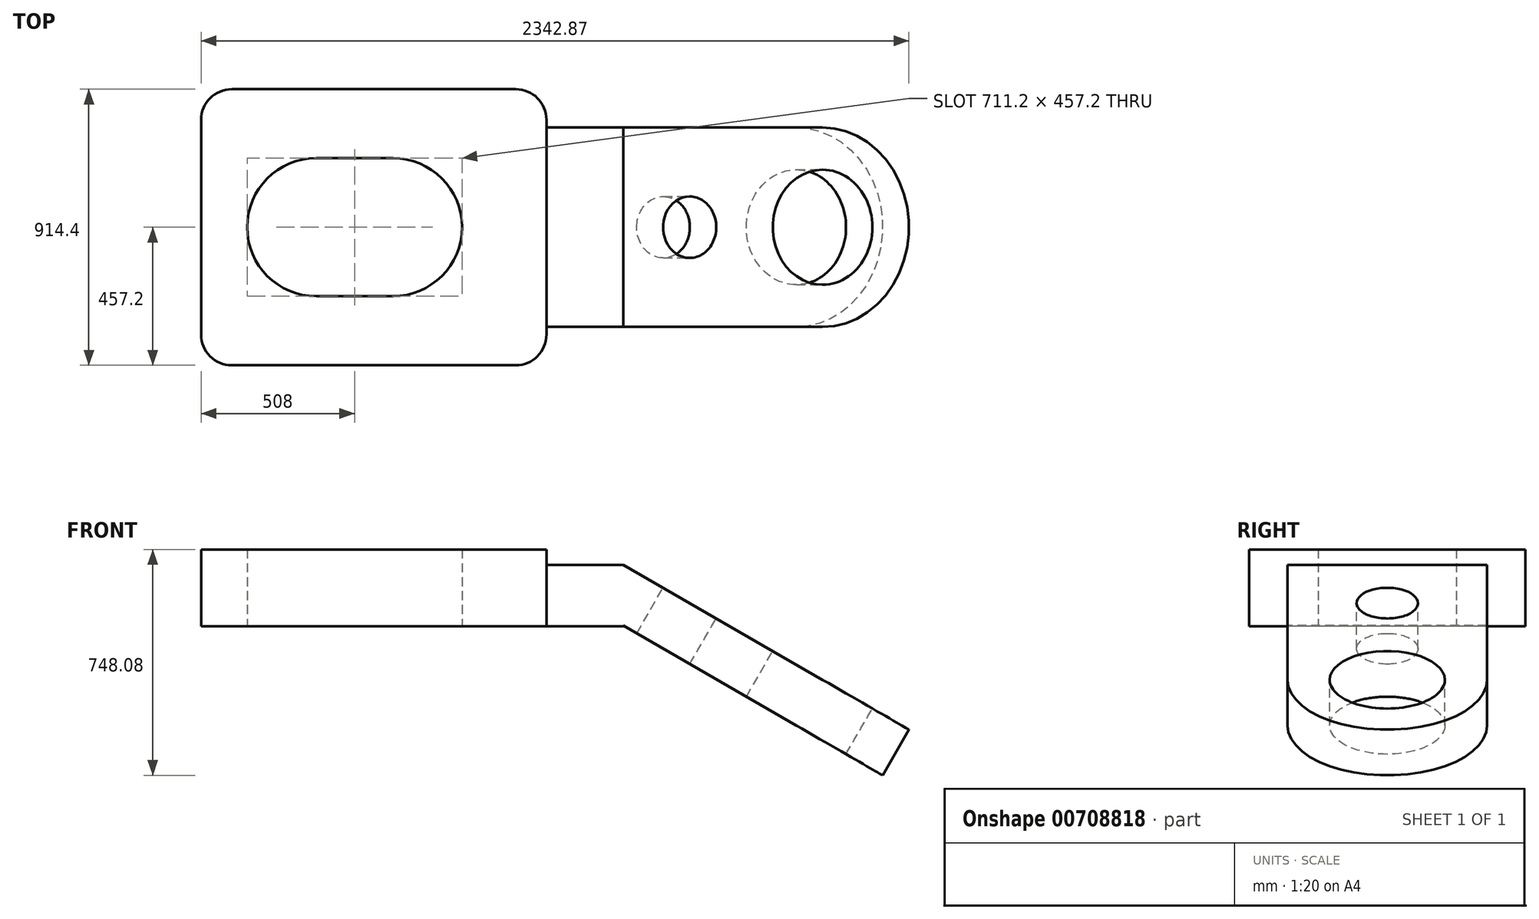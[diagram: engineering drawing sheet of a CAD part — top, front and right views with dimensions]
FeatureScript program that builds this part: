
annotation { "Feature Type Name" : "Feature", "Feature Type Description" : "" }
export const myFeature = defineFeature(function(context is Context, id is Id, definition is map)
    precondition{}
    {
        {
            var Q0;
            Q0=qCreatedBy(makeId("Top.planeOp"),FACE);
            var sketch = newSketch(context, id + "F0", { "sketchPlane" : qUnion([Q0])});
            skLineSegment(sketch, "E0.bottom", {"start": v(-254, 330.2) * mm, "end": v(0, 330.2) * mm});
            skLineSegment(sketch, "E0.top", {"start": v(-254, -330.2) * mm, "end": v(0, -330.2) * mm});
            skLineSegment(sketch, "E0.left", {"start": v(-254, 330.2) * mm, "end": v(-254, -330.2) * mm});
            skLineSegment(sketch, "E0.right", {"start": v(0, 330.2) * mm, "end": v(0, -330.2) * mm});
            skLineSegment(sketch, "E1", {"start": v(0, 0) * mm, "end": v(0, 851.18) * mm, "construction": true});
            skSolve(sketch);
        }
        {
            var Q0;
            Q0 = qSketchRegion(id + "F0", true);
            extrude(context, id + "F1", {"entities" : qUnion([Q0]), "oppositeDirection" : true, "depth" : 203.2 * mm, "offsetDistance" : 25.4 * mm});
        }
        {
            var Q0;
            Q0=makeQuery(id+"F1.opExtrude","CAP_FACE",FACE,{"disambiguationData":[OSD([sQuery(id+"F0.wireOp",EDGE,"E0.bottom"),sQuery(id+"F0.wireOp",EDGE,"E0.top"),sQuery(id+"F0.wireOp",EDGE,"E0.left"),sQuery(id+"F0.wireOp",EDGE,"E0.right")])],"isStart":true});
            var sketch = newSketch(context, id + "F2", { "sketchPlane" : qUnion([Q0])});
            skLineSegment(sketch, "E2.bottom", {"start": v(-254, 457.2) * mm, "end": v(-1397, 457.2) * mm});
            skLineSegment(sketch, "E2.top", {"start": v(-254, -457.2) * mm, "end": v(-1397, -457.2) * mm});
            skLineSegment(sketch, "E2.left", {"start": v(-254, 457.2) * mm, "end": v(-254, -457.2) * mm});
            skLineSegment(sketch, "E2.right", {"start": v(-1397, 457.2) * mm, "end": v(-1397, -457.2) * mm});
            skArc(sketch, "E3", {"start": v(-1016, 228.6) * mm, "mid": v(-1244.6, 0) * mm, "end": v(-1016, -228.6) * mm});
            skArc(sketch, "E4", {"start": v(-762, -228.6) * mm, "mid": v(-533.4, 0) * mm, "end": v(-762, 228.6) * mm});
            skLineSegment(sketch, "E5", {"start": v(-1016, 228.6) * mm, "end": v(-762, 228.6) * mm});
            skLineSegment(sketch, "E6", {"start": v(-1016, -228.6) * mm, "end": v(-762, -228.6) * mm});
            skSolve(sketch);
        }
        {
            var Q0;
            {var subQ3=sQuery(id+"F2.wireOp",EDGE,"E2.bottom");Q0=makeQuery(id+"F2.imprint","IMPRINT",FACE,{"disambiguationData":[TD([[makeQuery(id+"F2.imprint","IMPRINT",EDGE,{"derivedFrom":subQ3}),1.0]])]});}
            extrude(context, id + "F3", {"entities" : qUnion([Q0]), "operationType" : NewBodyOperationType.ADD, "depth" : 50.8 * mm, "offsetDistance" : 25.4 * mm, "hasSecondDirection" : true, "secondDirectionOppositeDirection" : true, "secondDirectionDepth" : 203.2 * mm});
        }
        {
            var Q0;
            Q0=makeQuery(id+"F3.opExtrude","SWEPT_EDGE",EDGE,{"disambiguationData":[OSD([sQuery(id+"F2.wireOp",EDGE,"E2.top"),sQuery(id+"F2.wireOp",EDGE,"E2.left")])]});
            var Q1;
            Q1=makeQuery(id+"F3.opExtrude","SWEPT_EDGE",EDGE,{"disambiguationData":[OSD([sQuery(id+"F2.wireOp",EDGE,"E2.bottom"),sQuery(id+"F2.wireOp",EDGE,"E2.left")])]});
            var Q2;
            Q2=makeQuery(id+"F3.opExtrude","SWEPT_EDGE",EDGE,{"disambiguationData":[OSD([sQuery(id+"F2.wireOp",EDGE,"E2.bottom"),sQuery(id+"F2.wireOp",EDGE,"E2.right")])]});
            var Q3;
            Q3=makeQuery(id+"F3.opExtrude","SWEPT_EDGE",EDGE,{"disambiguationData":[OSD([sQuery(id+"F2.wireOp",EDGE,"E2.top"),sQuery(id+"F2.wireOp",EDGE,"E2.right")])]});
            fillet(context, id + "F4", {"entities" : qUnion([Q0, Q1, Q2, Q3]), "radius" : 101.6 * mm, "tangentPropagation" : true, "allowEdgeOverflow" : false});
        }
        {
            var Q0;
            Q0=makeQuery(id+"F1.opExtrude","SWEPT_FACE",FACE,{"disambiguationData":[OSD([sQuery(id+"F0.wireOp",EDGE,"E0.top")])]});
            var sketch = newSketch(context, id + "F5", { "sketchPlane" : qUnion([Q0])});
            skLineSegment(sketch, "E7.bottom", {"start": v(0, 0) * mm, "end": v(945.87, -546.1) * mm});
            skLineSegment(sketch, "E7.top", {"start": v(-87.28, -151.18) * mm, "end": v(858.59, -697.28) * mm});
            skLineSegment(sketch, "E7.left", {"start": v(0, 0) * mm, "end": v(-87.28, -151.18) * mm});
            skLineSegment(sketch, "E7.right", {"start": v(945.87, -546.1) * mm, "end": v(858.59, -697.28) * mm});
            skLineSegment(sketch, "E8", {"start": v(0, 0) * mm, "end": v(991.08, 0) * mm, "construction": true});
            skSolve(sketch);
        }
        {
            var Q0;
            Q0 = qSketchRegion(id + "F5", true);
            extrude(context, id + "F6", {"entities" : qUnion([Q0]), "operationType" : NewBodyOperationType.ADD, "oppositeDirection" : true, "depth" : 660.4 * mm, "offsetDistance" : 25.4 * mm});
        }
        {
            var Q0;
            Q0=makeQuery(id+"F6.opExtrude","SWEPT_FACE",FACE,{"disambiguationData":[OSD([sQuery(id+"F5.wireOp",EDGE,"E7.bottom")])]});
            var sketch = newSketch(context, id + "F7", { "sketchPlane" : qUnion([Q0])});
            skArc(sketch, "E9", {"start": v(762, -330.2) * mm, "mid": v(1092.2, 0) * mm, "end": v(762, 330.2) * mm});
            skSolve(sketch);
        }
        {
            var Q0;
            {var subQ0=sQuery(id+"F7.wireOp",EDGE,"E9");var subQ1=sQuery(id+"F5.wireOp",EDGE,"E7.bottom");var subQ2=makeQuery(id+"F6.opExtrude","CAP_EDGE",EDGE,{"disambiguationData":[OSD([subQ1])],"isStart":true});var subQ3=makeQuery(id+"F7.imprint","INTERSECT",VERTEX,{"derivedFrom":[subQ2,subQ0]});Q0=makeQuery(id+"F7.imprint","IMPRINT",FACE,{"disambiguationData":[TD([[makeQuery(id+"F7.imprint","IMPRINT",EDGE,{"disambiguationData":[TD([[subQ3,-1.0]])],"derivedFrom":subQ0}),-1.0]])]});}
            var Q1;
            {var subQ0=sQuery(id+"F7.wireOp",EDGE,"E9");var subQ1=sQuery(id+"F5.wireOp",EDGE,"E7.bottom");var subQ2=makeQuery(id+"F6.opExtrude","CAP_EDGE",EDGE,{"disambiguationData":[OSD([subQ1])],"isStart":false});var subQ3=makeQuery(id+"F7.imprint","INTERSECT",VERTEX,{"derivedFrom":[subQ2,subQ0]});Q1=makeQuery(id+"F7.imprint","IMPRINT",FACE,{"disambiguationData":[TD([[makeQuery(id+"F7.imprint","IMPRINT",EDGE,{"disambiguationData":[TD([[subQ3,1.0]])],"derivedFrom":subQ0}),-1.0]])]});}
            extrude(context, id + "F8", {"entities" : qUnion([Q0, Q1]), "operationType" : NewBodyOperationType.REMOVE, "endBound" : BoundingType.THROUGH_ALL, "oppositeDirection" : true, "depth" : 25.4 * mm, "offsetDistance" : 25.4 * mm});
        }
        {
            var Q0;
            Q0=makeQuery(id+"F6.opExtrude","SWEPT_FACE",FACE,{"disambiguationData":[OSD([sQuery(id+"F5.wireOp",EDGE,"E7.bottom")])]});
            var sketch = newSketch(context, id + "F9", { "sketchPlane" : qUnion([Q0])});
            skCircle(sketch, "E10", {"center": v(762, 0) * mm, "radius": 190.5 * mm});
            skCircle(sketch, "E11", {"center": v(254, 0) * mm, "radius": 101.6 * mm});
            skSolve(sketch);
        }
        {
            var Q0;
            Q0 = qSketchRegion(id + "F9", true);
            extrude(context, id + "F10", {"entities" : qUnion([Q0]), "operationType" : NewBodyOperationType.REMOVE, "endBound" : BoundingType.THROUGH_ALL, "oppositeDirection" : true, "depth" : 25.4 * mm, "offsetDistance" : 25.4 * mm});
        }
    });
